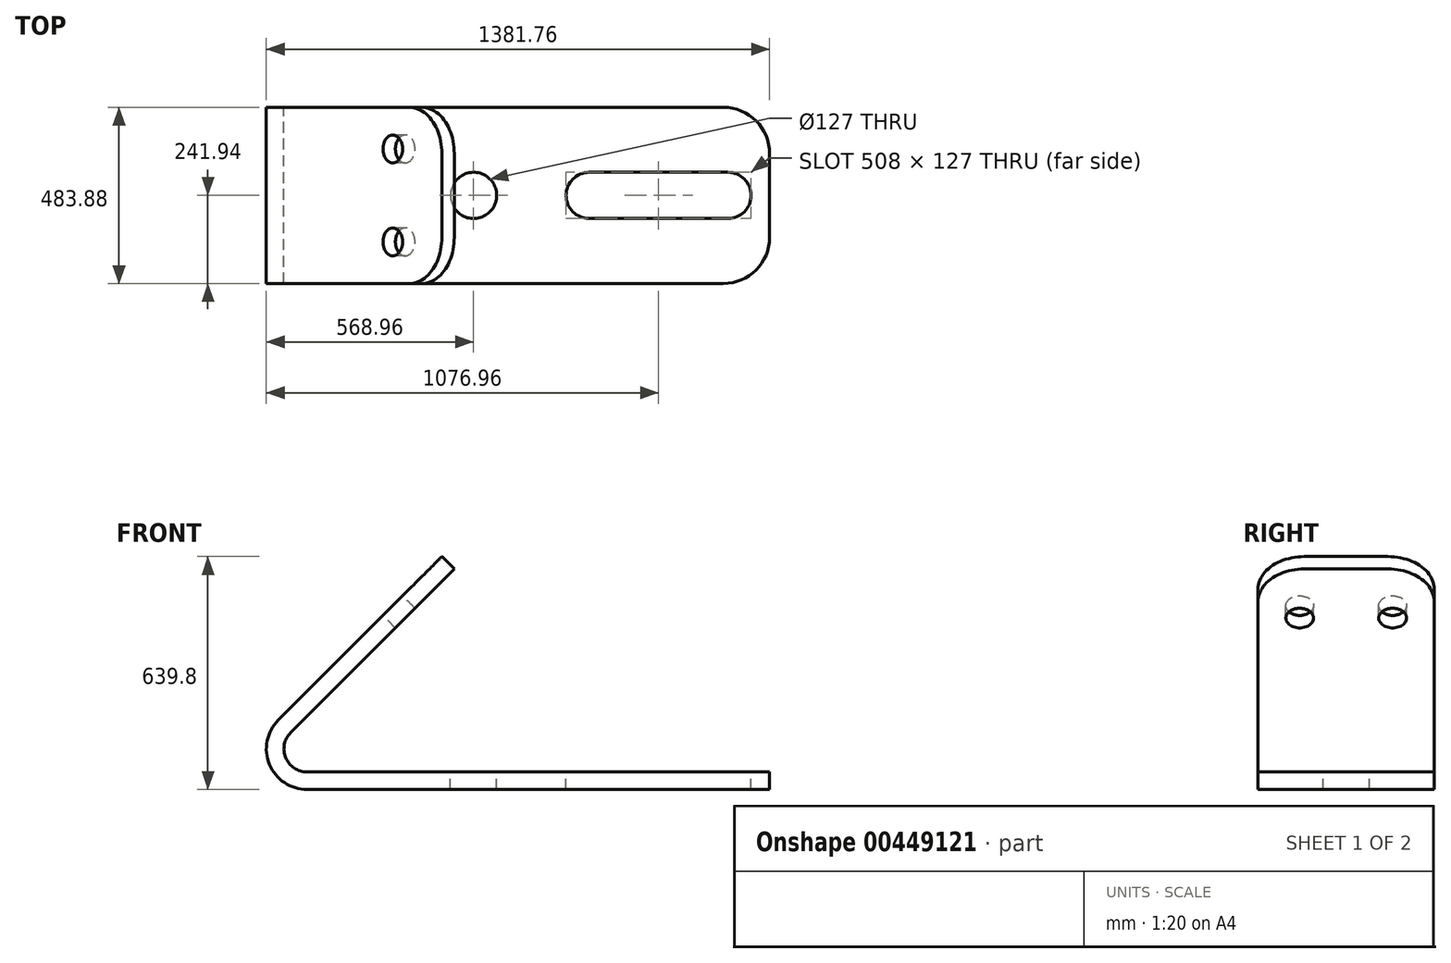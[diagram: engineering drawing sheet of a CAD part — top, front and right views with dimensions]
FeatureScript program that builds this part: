
annotation { "Feature Type Name" : "Feature", "Feature Type Description" : "" }
export const myFeature = defineFeature(function(context is Context, id is Id, definition is map)
    precondition{}
    {
        {
            var Q0;
            Q0=qCreatedBy(makeId("Front.planeOp"),FACE);
            var sketch = newSketch(context, id + "F0", { "sketchPlane" : qUnion([Q0])});
            skArc(sketch, "E0", {"start": v(-79.03, 79.03) * mm, "mid": v(-103.25, -42.77) * mm, "end": v(0, -111.76) * mm});
            skLineSegment(sketch, "E1", {"start": v(0, -111.76) * mm, "end": v(1270, -111.76) * mm});
            skLineSegment(sketch, "E2", {"start": v(-79.03, 79.03) * mm, "end": v(369.99, 528.04) * mm});
            skLineSegment(sketch, "E3.0", {"start": v(-44.9, 44.9) * mm, "end": v(404.11, 493.91) * mm});
            skLineSegment(sketch, "E4.0", {"start": v(0, -63.5) * mm, "end": v(1270, -63.5) * mm});
            skArc(sketch, "E5", {"start": v(-44.9, 44.9) * mm, "mid": v(-58.67, -24.3) * mm, "end": v(0, -63.5) * mm});
            skLineSegment(sketch, "E6", {"start": v(369.99, 528.04) * mm, "end": v(404.11, 493.91) * mm});
            skLineSegment(sketch, "E7", {"start": v(1270, -63.5) * mm, "end": v(1270, -111.76) * mm});
            skSolve(sketch);
        }
        {
            var Q0;
            Q0=makeQuery(id+"F0.imprint","IMPRINT",FACE,{"disambiguationData":[TD([[makeQuery(id+"F0.imprint","IMPRINT",EDGE,{"derivedFrom":sQuery(id+"F0.wireOp",EDGE,"E0")}),1.0]])]});
            extrude(context, id + "F1", {"entities" : qUnion([Q0]), "endBound" : BoundingType.SYMMETRIC, "depth" : 483.87 * mm});
        }
        {
            var Q0;
            Q0=makeQuery(id+"F1.opExtrude","SWEPT_FACE",FACE,{"disambiguationData":[OSD([sQuery(id+"F0.wireOp",EDGE,"E4.0")])]});
            var sketch = newSketch(context, id + "F2", { "sketchPlane" : qUnion([Q0])});
            skArc(sketch, "E8", {"start": v(774.7, 63.5) * mm, "mid": v(711.2, 0) * mm, "end": v(774.7, -63.5) * mm});
            skArc(sketch, "E9", {"start": v(1155.7, -63.5) * mm, "mid": v(1219.2, 0) * mm, "end": v(1155.7, 63.5) * mm});
            skLineSegment(sketch, "E10", {"start": v(774.7, 63.5) * mm, "end": v(1155.7, 63.5) * mm});
            skLineSegment(sketch, "E11", {"start": v(774.7, -63.5) * mm, "end": v(1155.7, -63.5) * mm});
            skCircle(sketch, "E12", {"center": v(457.2, 0) * mm, "radius": 63.5 * mm});
            skSolve(sketch);
        }
        {
            var Q0;
            Q0=makeQuery(id+"F2.imprint","IMPRINT",FACE,{"disambiguationData":[TD([[makeQuery(id+"F2.imprint","IMPRINT",EDGE,{"derivedFrom":sQuery(id+"F2.wireOp",EDGE,"E12")}),1.0]])]});
            var Q1;
            Q1=makeQuery(id+"F2.imprint","IMPRINT",FACE,{"disambiguationData":[TD([[makeQuery(id+"F2.imprint","IMPRINT",EDGE,{"derivedFrom":sQuery(id+"F2.wireOp",EDGE,"E8")}),1.0]])]});
            extrude(context, id + "F3", {"entities" : qUnion([Q0, Q1]), "operationType" : NewBodyOperationType.REMOVE, "endBound" : BoundingType.THROUGH_ALL, "oppositeDirection" : true, "depth" : 25.4 * mm});
        }
        {
            var Q0;
            Q0=makeQuery(id+"F1.opExtrude","CAP_EDGE",EDGE,{"disambiguationData":[OSD([sQuery(id+"F0.wireOp",EDGE,"E7")])],"isStart":false});
            var Q1;
            Q1=makeQuery(id+"F1.opExtrude","CAP_EDGE",EDGE,{"disambiguationData":[OSD([sQuery(id+"F0.wireOp",EDGE,"E7")])],"isStart":true});
            fillet(context, id + "F4", {"entities" : qUnion([Q0, Q1]), "radius" : 127 * mm, "tangentPropagation" : true, "allowEdgeOverflow" : false});
        }
        {
            var Q0;
            Q0=makeQuery(id+"F1.opExtrude","CAP_EDGE",EDGE,{"disambiguationData":[OSD([sQuery(id+"F0.wireOp",EDGE,"E6")])],"isStart":false});
            var Q1;
            Q1=makeQuery(id+"F1.opExtrude","CAP_EDGE",EDGE,{"disambiguationData":[OSD([sQuery(id+"F0.wireOp",EDGE,"E6")])],"isStart":true});
            fillet(context, id + "F5", {"entities" : qUnion([Q0, Q1]), "radius" : 127 * mm, "tangentPropagation" : true, "allowEdgeOverflow" : false});
        }
        {
            var Q0;
            Q0=makeQuery(id+"F1.opExtrude","SWEPT_FACE",FACE,{"disambiguationData":[OSD([sQuery(id+"F0.wireOp",EDGE,"E2")])]});
            var sketch = newSketch(context, id + "F6", { "sketchPlane" : qUnion([Q0])});
            skCircle(sketch, "E13", {"center": v(-127.64, 444.5) * mm, "radius": 38.1 * mm});
            skCircle(sketch, "E14", {"center": v(127.64, 444.5) * mm, "radius": 38.1 * mm});
            skSolve(sketch);
        }
        {
            var Q0;
            Q0=makeQuery(id+"F6.imprint","IMPRINT",FACE,{"disambiguationData":[TD([[makeQuery(id+"F6.imprint","IMPRINT",EDGE,{"derivedFrom":sQuery(id+"F6.wireOp",EDGE,"E13")}),1.0]])]});
            var Q1;
            Q1=makeQuery(id+"F6.imprint","IMPRINT",FACE,{"disambiguationData":[TD([[makeQuery(id+"F6.imprint","IMPRINT",EDGE,{"derivedFrom":sQuery(id+"F6.wireOp",EDGE,"E14")}),1.0]])]});
            extrude(context, id + "F7", {"entities" : qUnion([Q0, Q1]), "operationType" : NewBodyOperationType.REMOVE, "oppositeDirection" : true, "depth" : 76.2 * mm});
        }
    });
